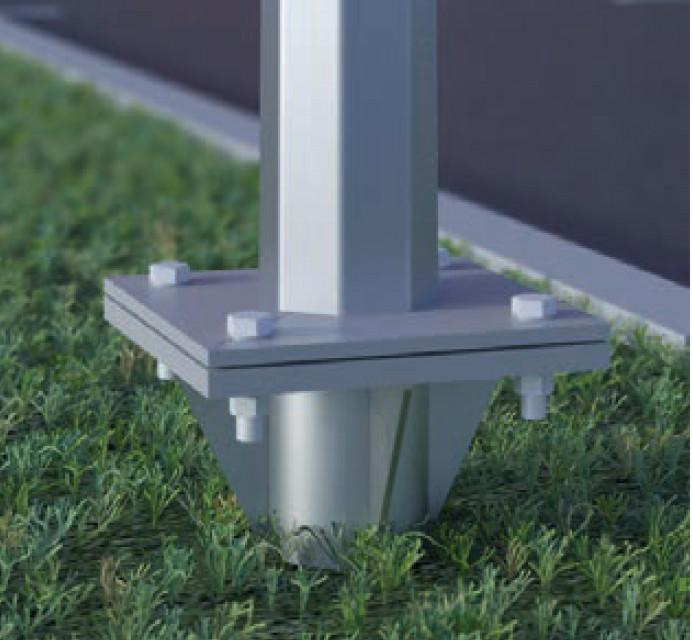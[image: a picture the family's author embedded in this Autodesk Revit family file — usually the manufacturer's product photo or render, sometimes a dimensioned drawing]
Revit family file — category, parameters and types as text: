
# Revit family: Комплект световой боллард Вертикаль
name_source: partatom
category: Осветительные приборы
revit_build: Autodesk Revit 2018 (Build: 20180423_1000(x64)
units: mm (PartAtom-declared; Revit-internal decimal feet)

## family parameters
Источник света = Нет
Общий = Нет
Основа = Грань
При загрузке вырезать с полостями = Да
Размер круглого соединителя = Использовать диаметр
Тип детали = Нормальный
Точка расчета площади = Нет

## types (2) — shared parameters
ADSK_Версия Revit = 2018
ADSK_Версия семейства = 1.01
ADSK_Единица измерения = шт.
ADSK_Завод-изготовитель = ООО «ОПОРА ИНЖИНИРИНГ»
ADSK_Количество = 1
ADSK_Обозначение = ГОСТ Р 1.4 – 2004, ГОСТ Р 1.5 – 2004, ГОСТ 16350-80, ГОСТ Р 1.12 – 2004, ГОСТ 8732-78, ГОСТ 10704-81, ГОСТ 11533-75, ГОСТ 27772-88*, ГОСТ 14771 -76, ГОСТ 23518-79, ГОСТ 14776-79*, ГОСТ 9.032-74* ЕСЗК, ГОСТ 9.307-89 ЕСЗК, ГОСТ 23118-99, ГОСТ 24297-87, ГОСТ 15.309-98, ГОСТ Р 15.201-2000
ADSK_Размер_Длина = 44 мм
ADSK_Размер_Ширина = 164 мм
H = 1000 мм
URL = https://opora-e.com
h1 = 500 мм
Вид опоры = К
Группа модели = Осветительный комплект
Изготовитель = ООО «ОПОРА ИНЖИНИРИНГ»
Класс Защиты = 1
Класс защиты от поражения электрическим током = I
Климатическая зона = III
Климатическое исполнение = У1
Наличие лючка = Нет
Наличие цоколя = Нет
Область использования = Садово-парковое освещение
Описание = Боллард с подсветкой
Отметка по умолчанию = 1219 мм
Покрытие = Порошковая покраска
Провод питания = Подземный
Сайт изготовителя = https://www.opora-e.com
Серия = Осветительный комплект
Способ установки = Ф
Срок службы = 25 лет
Телефон изготовителя = +7 (495) 785-50-28
Тип монтажной поверхности = грунт
Тип опоры = Несиловая
Тип продукции = Осветительный комплект
Характеристика заземления = Болт заземления М10
zero-valued in all types: ADSK_Масса, Максимальное горизонтальное усилие, Максимальный вес оборудования

## per-type parameters (varying)
| type | ADSK_Код изделия | ADSK_Материал | ADSK_Наименование краткое | Светильник |
| Световой боллард Вертикаль LED-15/727/YW360F в комплекте с анкерной закладной | 19719 | Сталь | Вертикаль LED-15/727/YW360F | GALAD Вертикаль LED : Световой боллард "Вертикаль" LED-15/727/YW360F в комплекте с анкерной закладной |
| Световой боллард Вертикаль LED-10/727/YW360F в комплекте с анкерной закладной | 19718 | Алюминий | Вертикаль LED-10/727/YW360F | GALAD Вертикаль LED : Световой боллард "Вертикаль" LED-10/727/YW360F в комплекте с анкерной закладной |

note: column(s) folded — value = type name in every type: ADSK_Марка, ADSK_Наименование
